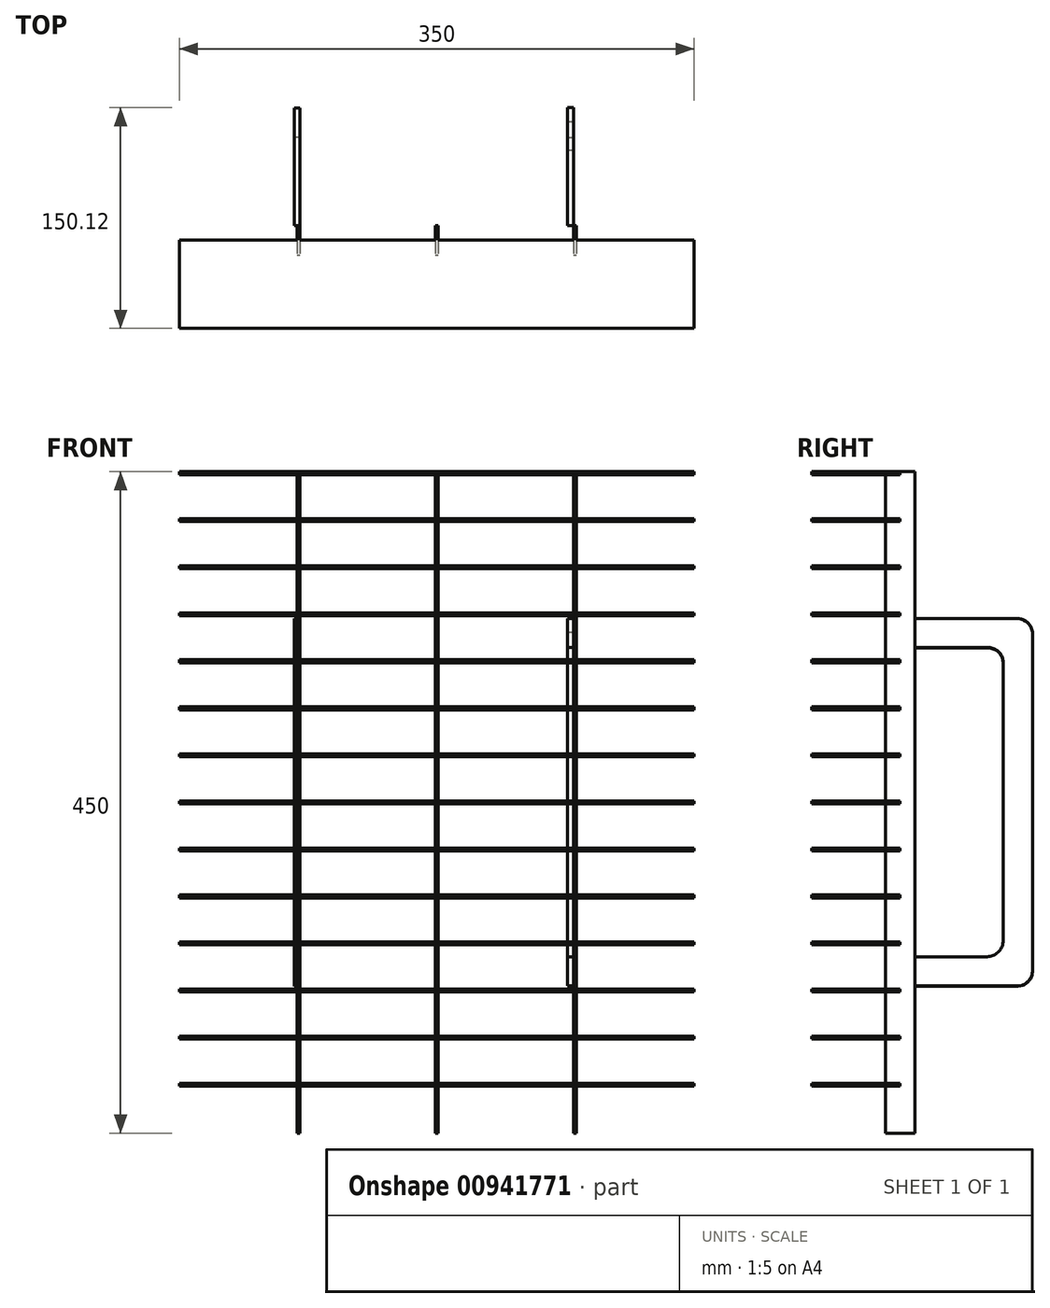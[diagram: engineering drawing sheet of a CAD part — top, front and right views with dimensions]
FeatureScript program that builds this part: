
annotation { "Feature Type Name" : "Feature", "Feature Type Description" : "" }
export const myFeature = defineFeature(function(context is Context, id is Id, definition is map)
    precondition{}
    {
        {
            var Q0;
            Q0=qCreatedBy(makeId("Front.planeOp"),FACE);
            var sketch = newSketch(context, id + "F0", { "sketchPlane" : qUnion([Q0])});
            skLineSegment(sketch, "E0.bottom", {"start": v(-350, 34) * mm, "end": v(0, 34) * mm});
            skLineSegment(sketch, "E0.top", {"start": v(-350, 32) * mm, "end": v(0, 32) * mm});
            skLineSegment(sketch, "E0.left", {"start": v(-350, 34) * mm, "end": v(-350, 32) * mm});
            skLineSegment(sketch, "E0.right", {"start": v(0, 34) * mm, "end": v(0, 32) * mm});
            skLineSegment(sketch, "E1.bottom", {"start": v(-350, 2) * mm, "end": v(0, 2) * mm});
            skLineSegment(sketch, "E1.top", {"start": v(-350, 0) * mm, "end": v(0, 0) * mm});
            skLineSegment(sketch, "E1.left", {"start": v(-350, 2) * mm, "end": v(-350, 0) * mm});
            skLineSegment(sketch, "E1.right", {"start": v(0, 2) * mm, "end": v(0, 0) * mm});
            skLineSegment(sketch, "E2.bottom", {"start": v(-350, 98) * mm, "end": v(0, 98) * mm});
            skLineSegment(sketch, "E2.top", {"start": v(-350, 96) * mm, "end": v(0, 96) * mm});
            skLineSegment(sketch, "E2.left", {"start": v(-350, 98) * mm, "end": v(-350, 96) * mm});
            skLineSegment(sketch, "E2.right", {"start": v(0, 98) * mm, "end": v(0, 96) * mm});
            skLineSegment(sketch, "E3.bottom", {"start": v(-350, 66) * mm, "end": v(0, 66) * mm});
            skLineSegment(sketch, "E3.top", {"start": v(-350, 64) * mm, "end": v(0, 64) * mm});
            skLineSegment(sketch, "E3.left", {"start": v(-350, 66) * mm, "end": v(-350, 64) * mm});
            skLineSegment(sketch, "E3.right", {"start": v(0, 66) * mm, "end": v(0, 64) * mm});
            skLineSegment(sketch, "E4.bottom", {"start": v(-350, 162) * mm, "end": v(0, 162) * mm});
            skLineSegment(sketch, "E4.top", {"start": v(-350, 160) * mm, "end": v(0, 160) * mm});
            skLineSegment(sketch, "E4.left", {"start": v(-350, 162) * mm, "end": v(-350, 160) * mm});
            skLineSegment(sketch, "E4.right", {"start": v(0, 162) * mm, "end": v(0, 160) * mm});
            skLineSegment(sketch, "E5.bottom", {"start": v(-350, 130) * mm, "end": v(0, 130) * mm});
            skLineSegment(sketch, "E5.top", {"start": v(-350, 128) * mm, "end": v(0, 128) * mm});
            skLineSegment(sketch, "E5.left", {"start": v(-350, 130) * mm, "end": v(-350, 128) * mm});
            skLineSegment(sketch, "E5.right", {"start": v(0, 130) * mm, "end": v(0, 128) * mm});
            skLineSegment(sketch, "E6.bottom", {"start": v(-350, 226) * mm, "end": v(0, 226) * mm});
            skLineSegment(sketch, "E6.top", {"start": v(-350, 224) * mm, "end": v(0, 224) * mm});
            skLineSegment(sketch, "E6.left", {"start": v(-350, 226) * mm, "end": v(-350, 224) * mm});
            skLineSegment(sketch, "E6.right", {"start": v(0, 226) * mm, "end": v(0, 224) * mm});
            skLineSegment(sketch, "E7.bottom", {"start": v(-350, 194) * mm, "end": v(0, 194) * mm});
            skLineSegment(sketch, "E7.top", {"start": v(-350, 192) * mm, "end": v(0, 192) * mm});
            skLineSegment(sketch, "E7.left", {"start": v(-350, 194) * mm, "end": v(-350, 192) * mm});
            skLineSegment(sketch, "E7.right", {"start": v(0, 194) * mm, "end": v(0, 192) * mm});
            skLineSegment(sketch, "E8.bottom", {"start": v(-350, 290) * mm, "end": v(0, 290) * mm});
            skLineSegment(sketch, "E8.top", {"start": v(-350, 288) * mm, "end": v(0, 288) * mm});
            skLineSegment(sketch, "E8.left", {"start": v(-350, 290) * mm, "end": v(-350, 288) * mm});
            skLineSegment(sketch, "E8.right", {"start": v(0, 290) * mm, "end": v(0, 288) * mm});
            skLineSegment(sketch, "E9.bottom", {"start": v(-350, 258) * mm, "end": v(0, 258) * mm});
            skLineSegment(sketch, "E9.top", {"start": v(-350, 256) * mm, "end": v(0, 256) * mm});
            skLineSegment(sketch, "E9.left", {"start": v(-350, 258) * mm, "end": v(-350, 256) * mm});
            skLineSegment(sketch, "E9.right", {"start": v(0, 258) * mm, "end": v(0, 256) * mm});
            skLineSegment(sketch, "E10.bottom", {"start": v(-350, 354) * mm, "end": v(0, 354) * mm});
            skLineSegment(sketch, "E10.top", {"start": v(-350, 352) * mm, "end": v(0, 352) * mm});
            skLineSegment(sketch, "E10.left", {"start": v(-350, 354) * mm, "end": v(-350, 352) * mm});
            skLineSegment(sketch, "E10.right", {"start": v(0, 354) * mm, "end": v(0, 352) * mm});
            skLineSegment(sketch, "E11.bottom", {"start": v(-350, 322) * mm, "end": v(0, 322) * mm});
            skLineSegment(sketch, "E11.top", {"start": v(-350, 320) * mm, "end": v(0, 320) * mm});
            skLineSegment(sketch, "E11.left", {"start": v(-350, 322) * mm, "end": v(-350, 320) * mm});
            skLineSegment(sketch, "E11.right", {"start": v(0, 322) * mm, "end": v(0, 320) * mm});
            skLineSegment(sketch, "E12.bottom", {"start": v(-350, 418) * mm, "end": v(0, 418) * mm});
            skLineSegment(sketch, "E12.top", {"start": v(-350, 416) * mm, "end": v(0, 416) * mm});
            skLineSegment(sketch, "E12.left", {"start": v(-350, 418) * mm, "end": v(-350, 416) * mm});
            skLineSegment(sketch, "E12.right", {"start": v(0, 418) * mm, "end": v(0, 416) * mm});
            skLineSegment(sketch, "E13.bottom", {"start": v(-350, 386) * mm, "end": v(0, 386) * mm});
            skLineSegment(sketch, "E13.top", {"start": v(-350, 384) * mm, "end": v(0, 384) * mm});
            skLineSegment(sketch, "E13.left", {"start": v(-350, 386) * mm, "end": v(-350, 384) * mm});
            skLineSegment(sketch, "E13.right", {"start": v(0, 386) * mm, "end": v(0, 384) * mm});
            skSolve(sketch);
        }
        {
            var Q0;
            Q0=makeQuery(id+"F0.imprint","IMPRINT",FACE,{"disambiguationData":[TD([[makeQuery(id+"F0.imprint","IMPRINT",EDGE,{"derivedFrom":sQuery(id+"F0.wireOp",EDGE,"E12.bottom")}),-1.0]])]});
            var Q1;
            Q1=makeQuery(id+"F0.imprint","IMPRINT",FACE,{"disambiguationData":[TD([[makeQuery(id+"F0.imprint","IMPRINT",EDGE,{"derivedFrom":sQuery(id+"F0.wireOp",EDGE,"E13.bottom")}),-1.0]])]});
            var Q2;
            Q2=makeQuery(id+"F0.imprint","IMPRINT",FACE,{"disambiguationData":[TD([[makeQuery(id+"F0.imprint","IMPRINT",EDGE,{"derivedFrom":sQuery(id+"F0.wireOp",EDGE,"E10.bottom")}),-1.0]])]});
            var Q3;
            Q3=makeQuery(id+"F0.imprint","IMPRINT",FACE,{"disambiguationData":[TD([[makeQuery(id+"F0.imprint","IMPRINT",EDGE,{"derivedFrom":sQuery(id+"F0.wireOp",EDGE,"E11.bottom")}),-1.0]])]});
            var Q4;
            Q4=makeQuery(id+"F0.imprint","IMPRINT",FACE,{"disambiguationData":[TD([[makeQuery(id+"F0.imprint","IMPRINT",EDGE,{"derivedFrom":sQuery(id+"F0.wireOp",EDGE,"E8.bottom")}),-1.0]])]});
            var Q5;
            Q5=makeQuery(id+"F0.imprint","IMPRINT",FACE,{"disambiguationData":[TD([[makeQuery(id+"F0.imprint","IMPRINT",EDGE,{"derivedFrom":sQuery(id+"F0.wireOp",EDGE,"E9.bottom")}),-1.0]])]});
            var Q6;
            Q6=makeQuery(id+"F0.imprint","IMPRINT",FACE,{"disambiguationData":[TD([[makeQuery(id+"F0.imprint","IMPRINT",EDGE,{"derivedFrom":sQuery(id+"F0.wireOp",EDGE,"E6.bottom")}),-1.0]])]});
            var Q7;
            Q7=makeQuery(id+"F0.imprint","IMPRINT",FACE,{"disambiguationData":[TD([[makeQuery(id+"F0.imprint","IMPRINT",EDGE,{"derivedFrom":sQuery(id+"F0.wireOp",EDGE,"E7.bottom")}),-1.0]])]});
            var Q8;
            Q8=makeQuery(id+"F0.imprint","IMPRINT",FACE,{"disambiguationData":[TD([[makeQuery(id+"F0.imprint","IMPRINT",EDGE,{"derivedFrom":sQuery(id+"F0.wireOp",EDGE,"E4.bottom")}),-1.0]])]});
            var Q9;
            Q9=makeQuery(id+"F0.imprint","IMPRINT",FACE,{"disambiguationData":[TD([[makeQuery(id+"F0.imprint","IMPRINT",EDGE,{"derivedFrom":sQuery(id+"F0.wireOp",EDGE,"E5.bottom")}),-1.0]])]});
            var Q10;
            Q10=makeQuery(id+"F0.imprint","IMPRINT",FACE,{"disambiguationData":[TD([[makeQuery(id+"F0.imprint","IMPRINT",EDGE,{"derivedFrom":sQuery(id+"F0.wireOp",EDGE,"E2.bottom")}),-1.0]])]});
            var Q11;
            Q11=makeQuery(id+"F0.imprint","IMPRINT",FACE,{"disambiguationData":[TD([[makeQuery(id+"F0.imprint","IMPRINT",EDGE,{"derivedFrom":sQuery(id+"F0.wireOp",EDGE,"E3.bottom")}),-1.0]])]});
            var Q12;
            Q12=makeQuery(id+"F0.imprint","IMPRINT",FACE,{"disambiguationData":[TD([[makeQuery(id+"F0.imprint","IMPRINT",EDGE,{"derivedFrom":sQuery(id+"F0.wireOp",EDGE,"E0.bottom")}),-1.0]])]});
            var Q13;
            Q13=makeQuery(id+"F0.imprint","IMPRINT",FACE,{"disambiguationData":[TD([[makeQuery(id+"F0.imprint","IMPRINT",EDGE,{"derivedFrom":sQuery(id+"F0.wireOp",EDGE,"E1.bottom")}),-1.0]])]});
            extrude(context, id + "F1", {"entities" : qUnion([Q0, Q1, Q2, Q3, Q4, Q5, Q6, Q7, Q8, Q9, Q10, Q11, Q12, Q13]), "depth" : 60 * mm, "offsetDistance" : 25 * mm});
        }
        {
            var Q0;
            Q0=makeQuery(id+"F1.opExtrude","SWEPT_FACE",FACE,{"disambiguationData":[OSD([sQuery(id+"F0.wireOp",EDGE,"E12.bottom")])]});
            var sketch = newSketch(context, id + "F2", { "sketchPlane" : qUnion([Q0])});
            skLineSegment(sketch, "E14.bottom", {"start": v(-270, 10) * mm, "end": v(-268, 10) * mm});
            skLineSegment(sketch, "E14.top", {"start": v(-270, -10) * mm, "end": v(-268, -10) * mm});
            skLineSegment(sketch, "E14.left", {"start": v(-270, 10) * mm, "end": v(-270, -10) * mm});
            skLineSegment(sketch, "E14.right", {"start": v(-268, 10) * mm, "end": v(-268, -10) * mm});
            skLineSegment(sketch, "E15.bottom", {"start": v(-82, 10) * mm, "end": v(-80, 10) * mm});
            skLineSegment(sketch, "E15.top", {"start": v(-82, -10) * mm, "end": v(-80, -10) * mm});
            skLineSegment(sketch, "E15.left", {"start": v(-82, 10) * mm, "end": v(-82, -10) * mm});
            skLineSegment(sketch, "E15.right", {"start": v(-80, 10) * mm, "end": v(-80, -10) * mm});
            skLineSegment(sketch, "E16.bottom", {"start": v(-176, 10) * mm, "end": v(-174, 10) * mm});
            skLineSegment(sketch, "E16.top", {"start": v(-176, -10) * mm, "end": v(-174, -10) * mm});
            skLineSegment(sketch, "E16.left", {"start": v(-176, 10) * mm, "end": v(-176, -10) * mm});
            skLineSegment(sketch, "E16.right", {"start": v(-174, 10) * mm, "end": v(-174, -10) * mm});
            skSolve(sketch);
        }
        {
            var Q0;
            Q0 = qSketchRegion(id + "F2", true);
            extrude(context, id + "F3", {"entities" : qUnion([Q0]), "operationType" : NewBodyOperationType.ADD, "oppositeDirection" : true, "depth" : 450 * mm, "offsetDistance" : 25 * mm});
        }
        {
            var Q0;
            Q0=makeQuery(id+"F3.opExtrude","SWEPT_FACE",FACE,{"disambiguationData":[OSD([sQuery(id+"F2.wireOp",EDGE,"E14.left")])]});
            var sketch = newSketch(context, id + "F4", { "sketchPlane" : qUnion([Q0])});
            skLineSegment(sketch, "E17.bottom", {"start": v(-10, 318) * mm, "end": v(-70, 318) * mm});
            skLineSegment(sketch, "E17.top", {"start": v(-10, 298) * mm, "end": v(-70, 298) * mm});
            skLineSegment(sketch, "E17.left", {"start": v(-10, 318) * mm, "end": v(-10, 298) * mm});
            skLineSegment(sketch, "E17.right", {"start": v(-70, 318) * mm, "end": v(-70, 298) * mm});
            skLineSegment(sketch, "E18.bottom", {"start": v(-10, 88) * mm, "end": v(-70, 88) * mm});
            skLineSegment(sketch, "E18.top", {"start": v(-10, 68) * mm, "end": v(-70, 68) * mm});
            skLineSegment(sketch, "E18.left", {"start": v(-10, 88) * mm, "end": v(-10, 68) * mm});
            skLineSegment(sketch, "E18.right", {"start": v(-70, 88) * mm, "end": v(-70, 68) * mm});
            skLineSegment(sketch, "E19", {"start": v(-70, 298) * mm, "end": v(-70, 88) * mm});
            skSolve(sketch);
        }
        {
            var Q0;
            {var subQ3=sQuery(id+"F4.wireOp",EDGE,"E17.left");Q0=makeQuery(id+"F4.imprint","IMPRINT",FACE,{"disambiguationData":[TD([[makeQuery(id+"F4.imprint","IMPRINT",EDGE,{"derivedFrom":subQ3}),-1.0]])]});}
            var sketch = newSketch(context, id + "F5", { "sketchPlane" : qUnion([Q0])});
            skLineSegment(sketch, "E20.bottom", {"start": v(-70, 318) * mm, "end": v(-10, 318) * mm});
            skLineSegment(sketch, "E20.top", {"start": v(-60, 298) * mm, "end": v(-10, 298) * mm});
            skLineSegment(sketch, "E20.right", {"start": v(-10, 318) * mm, "end": v(-10, 298) * mm});
            skLineSegment(sketch, "E21.bottom", {"start": v(-60, 88) * mm, "end": v(-10, 88) * mm});
            skLineSegment(sketch, "E21.top", {"start": v(-70, 68) * mm, "end": v(-10, 68) * mm});
            skLineSegment(sketch, "E21.right", {"start": v(-10, 88) * mm, "end": v(-10, 68) * mm});
            skLineSegment(sketch, "E22", {"start": v(-70, 288) * mm, "end": v(-70, 98) * mm});
            skLineSegment(sketch, "E23", {"start": v(-70, 318) * mm, "end": v(-80, 318) * mm});
            skLineSegment(sketch, "E24", {"start": v(-90, 308) * mm, "end": v(-90, 78) * mm});
            skLineSegment(sketch, "E25", {"start": v(-80, 68) * mm, "end": v(-70, 68) * mm});
            skPoint(sketch, "E26.visualSharp", {"position": v(-70, 298) * mm});
            skArc(sketch, "E26.filletArc", {"start": v(-60, 298) * mm, "mid": v(-67.07, 295.07) * mm, "end": v(-70, 288) * mm});
            skPoint(sketch, "E27.visualSharp", {"position": v(-70, 88) * mm});
            skArc(sketch, "E27.filletArc", {"start": v(-70, 98) * mm, "mid": v(-67.07, 90.93) * mm, "end": v(-60, 88) * mm});
            skPoint(sketch, "E28.visualSharp", {"position": v(-90, 68) * mm});
            skArc(sketch, "E28.filletArc", {"start": v(-90, 78) * mm, "mid": v(-87.07, 70.93) * mm, "end": v(-80, 68) * mm});
            skPoint(sketch, "E29.visualSharp", {"position": v(-90, 318) * mm});
            skArc(sketch, "E29.filletArc", {"start": v(-80, 318) * mm, "mid": v(-87.07, 315.07) * mm, "end": v(-90, 308) * mm});
            skSolve(sketch);
        }
        {
            var Q0;
            Q0=makeQuery(id+"F5.imprint","IMPRINT",FACE,{"disambiguationData":[TD([[makeQuery(id+"F5.imprint","IMPRINT",EDGE,{"derivedFrom":sQuery(id+"F5.wireOp",EDGE,"E20.bottom")}),-1.0]])]});
            extrude(context, id + "F6", {"entities" : qUnion([Q0]), "operationType" : NewBodyOperationType.ADD, "endBound" : BoundingType.SYMMETRIC, "oppositeDirection" : true, "depth" : 4 * mm, "offsetDistance" : 25 * mm});
        }
        {
            var Q0;
            Q0=makeQuery(id+"F3.opExtrude","SWEPT_FACE",FACE,{"disambiguationData":[OSD([sQuery(id+"F2.wireOp",EDGE,"E15.left")])]});
            var sketch = newSketch(context, id + "F7", { "sketchPlane" : qUnion([Q0])});
            skLineSegment(sketch, "E30", {"start": v(-10, 318.16) * mm, "end": v(-78.78, 318.16) * mm});
            skLineSegment(sketch, "E31", {"start": v(-10, 318.16) * mm, "end": v(-10, 298.25) * mm});
            skLineSegment(sketch, "E32", {"start": v(-10, 298.25) * mm, "end": v(-61.36, 298.25) * mm});
            skArc(sketch, "E33", {"start": v(-61.36, 298.25) * mm, "mid": v(-67.58, 294.82) * mm, "end": v(-70, 288.15) * mm});
            skArc(sketch, "E34", {"start": v(-78.78, 318.16) * mm, "mid": v(-86.15, 315.5) * mm, "end": v(-90.12, 308.74) * mm});
            skLineSegment(sketch, "E35", {"start": v(-90.12, 308.74) * mm, "end": v(-90.12, 78.69) * mm});
            skLineSegment(sketch, "E36", {"start": v(-70, 288.15) * mm, "end": v(-70, 98.05) * mm});
            skLineSegment(sketch, "E37", {"start": v(-10, 68.1) * mm, "end": v(-80.71, 68.1) * mm});
            skLineSegment(sketch, "E38", {"start": v(-10, 68.1) * mm, "end": v(-10, 88.04) * mm});
            skLineSegment(sketch, "E39", {"start": v(-10, 88.04) * mm, "end": v(-59.21, 88.04) * mm});
            skArc(sketch, "E40", {"start": v(-70, 98.05) * mm, "mid": v(-66.57, 90.93) * mm, "end": v(-59.21, 88.04) * mm});
            skArc(sketch, "E41", {"start": v(-90.12, 78.69) * mm, "mid": v(-87.43, 71.6) * mm, "end": v(-80.71, 68.1) * mm});
            skSolve(sketch);
        }
        {
            var Q0;
            Q0 = qSketchRegion(id + "F7", true);
            extrude(context, id + "F8", {"entities" : qUnion([Q0]), "depth" : 4 * mm, "offsetDistance" : 25 * mm});
        }
    });
